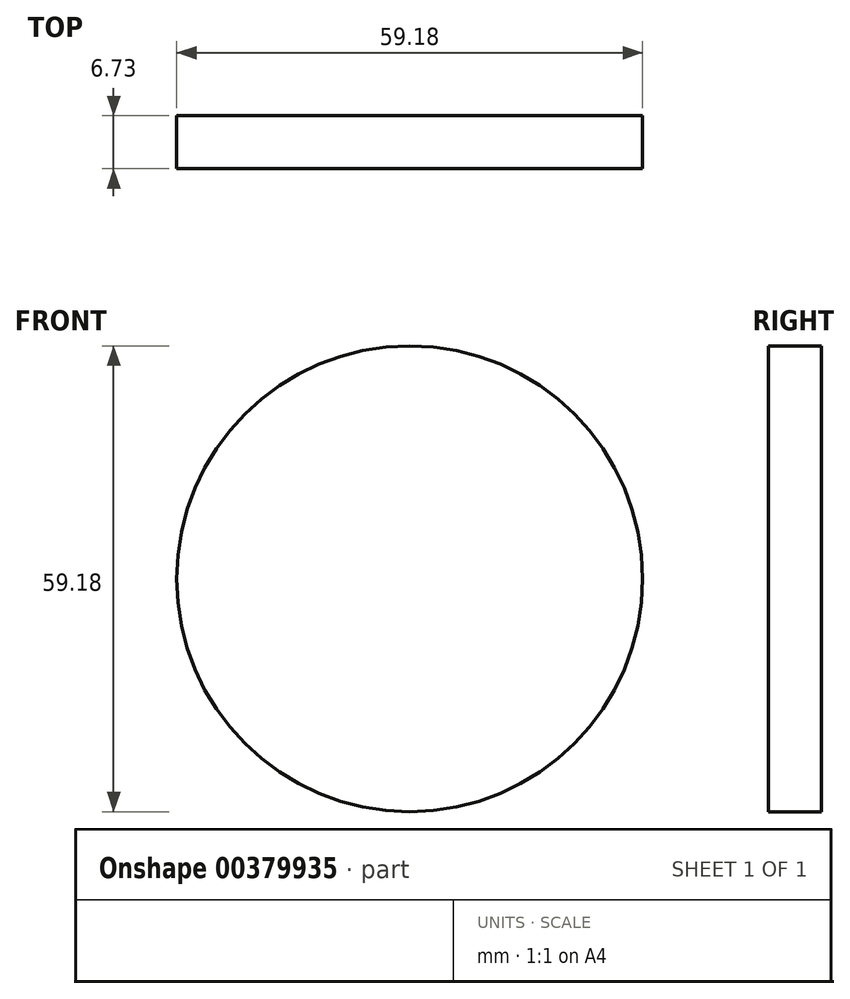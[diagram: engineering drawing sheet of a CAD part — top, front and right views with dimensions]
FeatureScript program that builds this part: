
annotation { "Feature Type Name" : "Feature", "Feature Type Description" : "" }
export const myFeature = defineFeature(function(context is Context, id is Id, definition is map)
    precondition{}
    {
        {
            var Q0;
            Q0=qCreatedBy(makeId("Front.planeOp"),FACE);
            var sketch = newSketch(context, id + "F0", { "sketchPlane" : qUnion([Q0])});
            skCircle(sketch, "E0", {"center": v(0, 0) * mm, "radius": 29.6 * mm});
            skSolve(sketch);
        }
        {
            var Q0;
            Q0=makeQuery(id+"F0.imprint","IMPRINT",FACE,{"disambiguationData":[TD([[makeQuery(id+"F0.imprint","IMPRINT",EDGE,{"derivedFrom":sQuery(id+"F0.wireOp",EDGE,"E0")}),1.0]])]});
            extrude(context, id + "F1", {"entities" : qUnion([Q0]), "depth" : 6.73 * mm});
        }
    });
